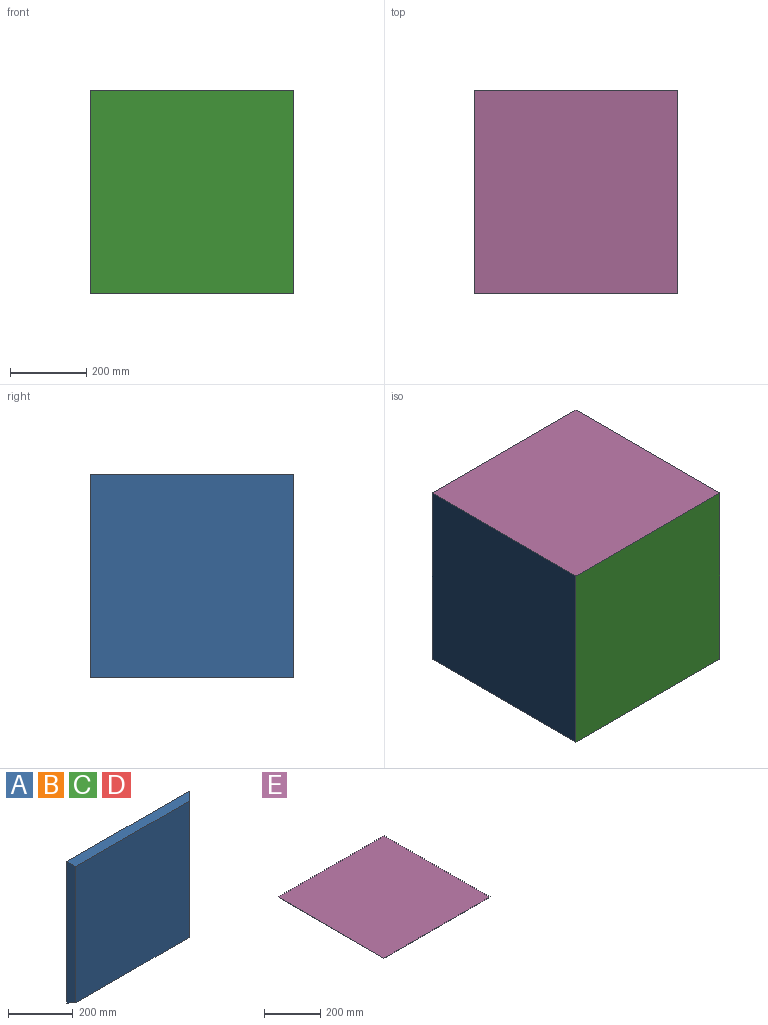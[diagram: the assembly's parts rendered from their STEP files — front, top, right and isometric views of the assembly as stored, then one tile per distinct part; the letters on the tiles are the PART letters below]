
ASSEMBLY  parts=5 mates=4
PART A: 6 faces, bbox 533.4x19.1x533.4 mm
  f0: plane 533.4x19.05mm, normal (0,0,-1), area 9798.4mm2, adj f1,f2,f3,f5
  f1: plane 514.35x495.3mm, normal (0,-1,0), area 254757.6mm2, adj f0,f3,f4,f5
  f2: plane 533.4x533.4mm, normal (0,1,0), area 284515.6mm2, adj f0,f3,f4,f5
  f3: plane 533.4x19.05mm, normal (-0.71,-0.71,0), area 14113.6mm2, adj f0,f1,f2,f4
  f4: plane 533.4x19.05mm, normal (0,-0.71,0.71), area 13857mm2, adj f1,f2,f3,f5
  f5: plane 533.4x19.05mm, normal (0.71,-0.71,0), area 14113.6mm2, adj f0,f1,f2,f4
PART B: same geometry as A
PART C: same geometry as A
PART D: same geometry as A
PART E: 6 faces, bbox 533.4x533.4x19.1 mm
  f0: plane 533.4x533.4mm, normal (0,0,1), area 284515.6mm2, adj f2,f3,f4,f5
  f1: plane 495.3x495.3mm, normal (0,0,-1), area 245322.1mm2, adj f2,f3,f4,f5
  f2: plane 533.4x19.05mm, normal (0,-0.71,-0.71), area 13857mm2, adj f0,f1,f3,f4
  f3: plane 533.4x19.05mm, normal (-0.71,0,-0.71), area 13857mm2, adj f0,f1,f2,f5
  f4: plane 533.4x19.05mm, normal (0.71,0,-0.71), area 13857mm2, adj f0,f1,f2,f5
  f5: plane 533.4x19.05mm, normal (0,0.71,-0.71), area 13857mm2, adj f0,f1,f3,f4
PLACE A rot(axis=(0,0,1),90deg) t=(-610.11,15.91,1.46)mm
PLACE B t=(-345.06,284.27,1.46)mm
PLACE C rot(axis=(0,0,-1),180deg) t=(-341.75,-249.13,1.46)mm
PLACE D rot(axis=(0,0,-1),90deg) t=(-76.71,19.22,1.46)mm
PLACE E t=(-351.67,-30.34,314.23)mm
MATE fastened D.f4 <-> E.f4  axis (-0.71,0,0.71) through (-76.71,284.27,333.28)mm
MATE fastened B.f4 <-> E.f5  axis (0,-0.71,0.71) through (-76.71,284.27,333.28)mm
MATE fastened C.f4 <-> E.f2  axis (0,0.71,0.71) through (-76.71,-249.13,333.28)mm
MATE fastened A.f4 <-> E.f3  axis (0.71,0,0.71) through (-610.11,-249.13,333.28)mm
